# Revit family: Workstations-Teknion-BGMTH-Run-Off_with_Glass_Top-R2015
name_source: partatom
category: Furniture
revit_build: Autodesk Revit Architecture 2015 (Build: 20140323_1530(x64)
units: mm (PartAtom-declared; Revit-internal decimal feet)

## types (2) — shared parameters
Assembly Code = E2020200
Manufacturer = Teknion
Manufacturer Fax = 416.661.4586
Part Number = BGMTH
Product Documentation Link = http://www.teknion.com
Product Line = Expansion Casegoods
Product Page URL = http://www.teknion.com
Series = Expansion Casegoods
Sustainability Data = http://www.teknion.com
URL = www.teknion.com
Unit Weight URL = http://www.teknion.com
Warranty = http://www.teknion.com

## per-type parameters (varying)
| type | Description | Model | With Bevel Base | With Dual Square Post Legs |
| Bevel Base | Run-Off with Glass Top – High Secondary Desk, Bevel Base | BGMTHB____10 | Yes | No |
| Dual Square Post Legs | Run-Off with Glass Top – High Secondary Desk, Dual Square Post Legs | BGMTHS____10 | No | Yes |

## geometry (parser evidence)
native form markers: Blend x148, Sweep x3
no freeform markers — native parametric forms only
